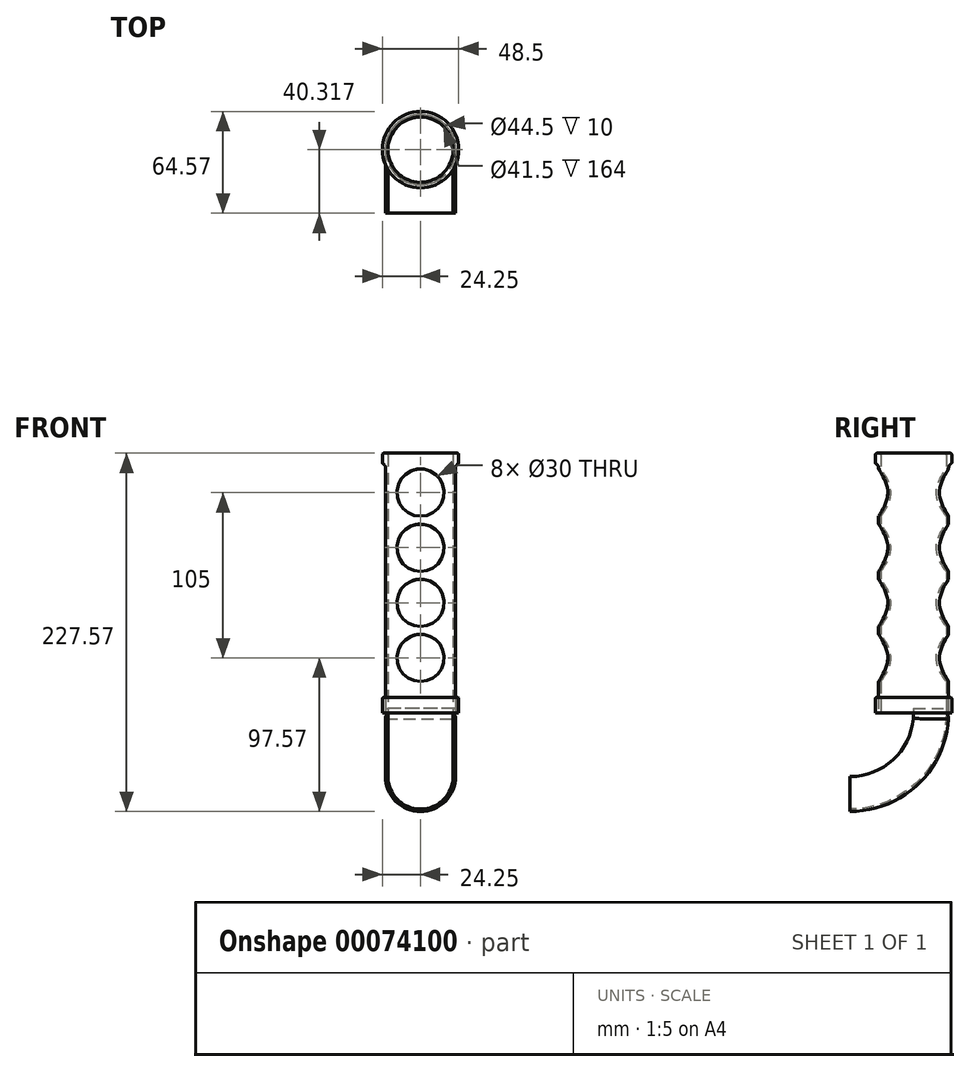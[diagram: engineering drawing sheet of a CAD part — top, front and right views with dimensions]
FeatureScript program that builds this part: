
annotation { "Feature Type Name" : "Feature", "Feature Type Description" : "" }
export const myFeature = defineFeature(function(context is Context, id is Id, definition is map)
    precondition{}
    {
        {
            var Q0;
            Q0=qCreatedBy(makeId("Top.planeOp"),FACE);
            var sketch = newSketch(context, id + "F0", { "sketchPlane" : qUnion([Q0])});
            skCircle(sketch, "E0", {"center": v(0, 40.32) * mm, "radius": 20.75 * mm});
            skCircle(sketch, "E1", {"center": v(0, 40.32) * mm, "radius": 22.25 * mm});
            skSolve(sketch);
        }
        {
            var Q0;
            Q0=makeQuery(id+"F0.imprint","IMPRINT",FACE,{"disambiguationData":[TD([[makeQuery(id+"F0.imprint","IMPRINT",EDGE,{"derivedFrom":sQuery(id+"F0.wireOp",EDGE,"E0")}),-1.0]])]});
            extrude(context, id + "F1", {"entities" : qUnion([Q0]), "depth" : 160 * mm});
        }
        {
            var Q0;
            Q0=qCreatedBy(makeId("Front.planeOp"),FACE);
            var sketch = newSketch(context, id + "F2", { "sketchPlane" : qUnion([Q0])});
            skCircle(sketch, "E2", {"center": v(0, 70) * mm, "radius": 15 * mm});
            skCircle(sketch, "E3", {"center": v(0, 105) * mm, "radius": 15 * mm});
            skCircle(sketch, "E4", {"center": v(0, 140) * mm, "radius": 15 * mm});
            skCircle(sketch, "E5", {"center": v(0, 35) * mm, "radius": 15 * mm});
            skLineSegment(sketch, "E6", {"start": v(0, 35) * mm, "end": v(0, 0) * mm, "construction": true});
            skSolve(sketch);
        }
        {
            var Q0;
            Q0=makeQuery(id+"F2.imprint","IMPRINT",FACE,{"disambiguationData":[TD([[makeQuery(id+"F2.imprint","IMPRINT",EDGE,{"derivedFrom":sQuery(id+"F2.wireOp",EDGE,"E4")}),1.0]])]});
            var Q1;
            Q1=makeQuery(id+"F2.imprint","IMPRINT",FACE,{"disambiguationData":[TD([[makeQuery(id+"F2.imprint","IMPRINT",EDGE,{"derivedFrom":sQuery(id+"F2.wireOp",EDGE,"E3")}),1.0]])]});
            var Q2;
            Q2=makeQuery(id+"F2.imprint","IMPRINT",FACE,{"disambiguationData":[TD([[makeQuery(id+"F2.imprint","IMPRINT",EDGE,{"derivedFrom":sQuery(id+"F2.wireOp",EDGE,"E2")}),1.0]])]});
            var Q3;
            Q3=makeQuery(id+"F2.imprint","IMPRINT",FACE,{"disambiguationData":[TD([[makeQuery(id+"F2.imprint","IMPRINT",EDGE,{"derivedFrom":sQuery(id+"F2.wireOp",EDGE,"E5")}),1.0]])]});
            extrude(context, id + "F3", {"entities" : qUnion([Q0, Q1, Q2, Q3]), "operationType" : NewBodyOperationType.REMOVE, "endBound" : BoundingType.THROUGH_ALL, "oppositeDirection" : true, "depth" : 25 * mm});
        }
        {
            var Q0;
            Q0=makeQuery(id+"F1.opExtrude","CAP_FACE",FACE,{"disambiguationData":[OSD([sQuery(id+"F0.wireOp",EDGE,"E0"),sQuery(id+"F0.wireOp",EDGE,"E1")])],"isStart":true});
            var sketch = newSketch(context, id + "F4", { "sketchPlane" : qUnion([Q0])});
            skLineSegment(sketch, "E7", {"start": v(0, -40.32) * mm, "end": v(22.25, -40.32) * mm, "construction": true});
            skLineSegment(sketch, "E8", {"start": v(0, -18.07) * mm, "end": v(0, -62.57) * mm, "construction": true});
            skLineSegment(sketch, "E9", {"start": v(0, -40.32) * mm, "end": v(-22.25, -40.32) * mm, "construction": true});
            skArc(sketch, "E10", {"start": v(-22.25, -40.32) * mm, "mid": v(0, -62.57) * mm, "end": v(22.25, -40.32) * mm});
            skArc(sketch, "E11", {"start": v(-20.75, -40.32) * mm, "mid": v(0, -61.07) * mm, "end": v(20.75, -40.32) * mm});
            skLineSegment(sketch, "E12", {"start": v(-22.25, -40.32) * mm, "end": v(-20.75, -40.32) * mm});
            skLineSegment(sketch, "E13", {"start": v(20.75, -40.32) * mm, "end": v(22.25, -40.32) * mm});
            skSolve(sketch);
        }
        {
            var Q0;
            Q0=qCreatedBy(makeId("Right.planeOp"),FACE);
            var sketch = newSketch(context, id + "F5", { "sketchPlane" : qUnion([Q0])});
            skArc(sketch, "E14", {"start": v(0, -62.57) * mm, "mid": v(44.24, -44.24) * mm, "end": v(62.57, 0) * mm});
            skSolve(sketch);
        }
        {
            var Q0;
            Q0=makeQuery(id+"F4.imprint","IMPRINT",FACE,{"disambiguationData":[TD([[makeQuery(id+"F4.imprint","IMPRINT",EDGE,{"derivedFrom":sQuery(id+"F4.wireOp",EDGE,"E10")}),-1.0]])]});
            var Q1;
            Q1=sQuery(id+"F5.wireOp",EDGE,"E14");
            sweep(context, id + "F6", {"profiles" : qUnion([Q0]), "path" : qUnion([Q1])});
        }
        {
            var Q0;
            Q0=makeQuery(id+"F6.opSweep","CAP_FACE",FACE,{"disambiguationData":[OSD([sQuery(id+"F4.wireOp",EDGE,"E10"),sQuery(id+"F4.wireOp",EDGE,"E11"),sQuery(id+"F4.wireOp",EDGE,"E12"),sQuery(id+"F4.wireOp",EDGE,"E13"),sQuery(id+"F5.wireOp",VERTEX,"E14.end")])],"isStart":true});
            var sketch = newSketch(context, id + "F7", { "sketchPlane" : qUnion([Q0])});
            skCircle(sketch, "E15", {"center": v(0, 40.32) * mm, "radius": 22.25 * mm});
            skCircle(sketch, "E16", {"center": v(0, 40.32) * mm, "radius": 24.25 * mm});
            skLineSegment(sketch, "E17", {"start": v(-22.25, 40.32) * mm, "end": v(-24.25, 40.32) * mm});
            skLineSegment(sketch, "E18", {"start": v(22.25, 40.32) * mm, "end": v(24.25, 40.32) * mm});
            skSolve(sketch);
        }
        {
            var Q0;
            Q0 = qSketchRegion(id + "F7", true);
            extrude(context, id + "F8", {"entities" : qUnion([Q0]), "depth" : 10 * mm});
        }
        {
            var Q0;
            Q0=makeQuery(id+"F6.opSweep","CAP_FACE",FACE,{"disambiguationData":[OSD([sQuery(id+"F4.wireOp",EDGE,"E10"),sQuery(id+"F4.wireOp",EDGE,"E11"),sQuery(id+"F4.wireOp",EDGE,"E12"),sQuery(id+"F4.wireOp",EDGE,"E13"),sQuery(id+"F5.wireOp",VERTEX,"E14.end")])],"isStart":true});
            extrude(context, id + "F9", {"entities" : qUnion([Q0]), "depth" : 3 * mm});
        }
        {
            var Q0;
            Q0=makeQuery(id+"F6.opSweep","CAP_EDGE",EDGE,{"disambiguationData":[OSD([sQuery(id+"F4.wireOp",EDGE,"E10"),sQuery(id+"F5.wireOp",VERTEX,"E14.end")])],"isStart":true});
            fillet(context, id + "F10", {"entities" : qUnion([Q0]), "radius" : 5 * mm, "tangentPropagation" : true, "allowEdgeOverflow" : false});
        }
        {
            var Q0;
            Q0=makeQuery(id+"F6.opSweep","SWEPT_BODY",BODY,{"disambiguationData":[OSD([sQuery(id+"F4.wireOp",EDGE,"E10"),sQuery(id+"F4.wireOp",EDGE,"E11"),sQuery(id+"F4.wireOp",EDGE,"E12"),sQuery(id+"F4.wireOp",EDGE,"E13"),sQuery(id+"F5.wireOp",EDGE,"E14")])]});
            var Q1;
            Q1=makeQuery(id+"F1.opExtrude","SWEPT_BODY",BODY,{"disambiguationData":[OSD([sQuery(id+"F0.wireOp",EDGE,"E0"),sQuery(id+"F0.wireOp",EDGE,"E1")])]});
            booleanBodies(context, id + "F11", {"operationType" : BooleanOperationType.SUBTRACTION, "tools" : qUnion([Q0]), "targets" : qUnion([Q1]), "keepTools" : true});
        }
        {
            var Q0;
            Q0=makeQuery(id+"F1.opExtrude","CAP_FACE",FACE,{"disambiguationData":[OSD([sQuery(id+"F0.wireOp",EDGE,"E0"),sQuery(id+"F0.wireOp",EDGE,"E1")])],"isStart":false});
            var sketch = newSketch(context, id + "F12", { "sketchPlane" : qUnion([Q0])});
            skCircle(sketch, "E19", {"center": v(0, 40.32) * mm, "radius": 24.25 * mm});
            skCircle(sketch, "E20", {"center": v(0, 40.32) * mm, "radius": 20.75 * mm});
            skSolve(sketch);
        }
        {
            var Q0;
            Q0 = qSketchRegion(id + "F12", true);
            extrude(context, id + "F13", {"entities" : qUnion([Q0]), "operationType" : NewBodyOperationType.ADD, "depth" : 5 * mm, "hasSecondDirection" : true, "secondDirectionOppositeDirection" : true, "secondDirectionDepth" : 1.5 * mm});
        }
        {
            var Q0;
            Q0=makeQuery(id+"F13.boolean.opBoolean","INTERSECT",EDGE,{"derivedFrom":[makeQuery(id+"F1.opExtrude","SWEPT_FACE",FACE,{"disambiguationData":[OSD([sQuery(id+"F0.wireOp",EDGE,"E1")])]}),makeQuery(id+"F13.opExtrude","CAP_FACE",FACE,{"disambiguationData":[OSD([sQuery(id+"F12.wireOp",EDGE,"E19"),sQuery(id+"F12.wireOp",EDGE,"E20")])],"isStart":true})]});
            fillet(context, id + "F14", {"entities" : qUnion([Q0]), "radius" : 3 * mm, "tangentPropagation" : true, "allowEdgeOverflow" : false});
        }
        {
            var Q0;
            Q0=makeQuery(id+"F13.opExtrude","CAP_EDGE",EDGE,{"disambiguationData":[OSD([sQuery(id+"F12.wireOp",EDGE,"E19")])],"isStart":false});
            var Q1;
            Q1=makeQuery(id+"F13.opExtrude","CAP_EDGE",EDGE,{"disambiguationData":[OSD([sQuery(id+"F12.wireOp",EDGE,"E20")])],"isStart":false});
            var Q2;
            {var subQ0=sQuery(id+"F12.wireOp",EDGE,"E19");Q2=makeQuery(id+"F14.opFillet","BLEND_EDGE",EDGE,{"blendedFrom":[makeQuery(id+"F13.boolean.opBoolean","INTERSECT",EDGE,{"derivedFrom":[makeQuery(id+"F1.opExtrude","SWEPT_FACE",FACE,{"disambiguationData":[OSD([sQuery(id+"F0.wireOp",EDGE,"E1")])]}),makeQuery(id+"F13.opExtrude","CAP_FACE",FACE,{"disambiguationData":[OSD([subQ0,sQuery(id+"F12.wireOp",EDGE,"E20")])],"isStart":true})]}),makeQuery(id+"F13.opExtrude","SWEPT_FACE",FACE,{"disambiguationData":[OSD([subQ0])]})],"blendedInto":[makeQuery(id+"F13.opExtrude","SWEPT_FACE",FACE,{"disambiguationData":[OSD([subQ0])]})]});}
            var Q3;
            Q3=makeQuery(id+"F8.opExtrude","CAP_EDGE",EDGE,{"disambiguationData":[OSD([sQuery(id+"F7.wireOp",EDGE,"E16")])],"isStart":false});
            fillet(context, id + "F15", {"entities" : qUnion([Q0, Q1, Q2, Q3]), "radius" : 1 * mm, "tangentPropagation" : true, "allowEdgeOverflow" : false});
        }
    });
